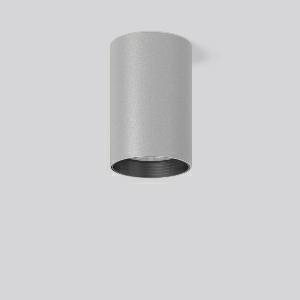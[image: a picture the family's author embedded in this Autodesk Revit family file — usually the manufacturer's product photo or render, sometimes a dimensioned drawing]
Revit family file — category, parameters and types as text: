
# Revit family: heledon_maxi_a_931222_004_1_76_c6c2
name_source: partatom
category: Lighting Fixtures
units: mm (PartAtom-declared; Revit-internal decimal feet)

## family parameters
Cut with Voids When Loaded = No
Host = Face
Light Source = No
Part Type = Normal
Room Calculation Point = No
Round Connector Dimension = Use Diameter
Shared = No

## types (1)
- HELEDON maxi A (1 x LED Modul 940, 2950 lm, 4000)
    Apparent Load = 25 VA
    Approval mark = CE
    CIE Flux Codes = 96 100 100 100 100
    Color Rendering = 92
    Color Temperature = 4000
    Default Elevation = 1800 mm
    Description = Series: HELEDON maxi
Cylindrical surface-mounted downlight. Housing: die-cast aluminium, powder-coated. Internal ceiling frame polycarbonate with bayonet mounting. Black plastic ring and recessed LED to prevent glare from the side. Optical assembly with lens made of plastic (polycarbonate) for the best homogeneous light distribution - can be changed without tools. Best colour rendering index Ra>90. Suitable for Ceiling mounting. Easy installation with a separate ceiling frame with bayonet mounting and plug connection. Driver integrated. Connected via plug-in connector. High quality converter without flickering and stroboscopic effect. The following accessories can be mounted without use of tools: interchangeable lenses, decorative glasses, honeycomb louvre, clear and frosted diffusers, white interchangeable plastic ring. 
Colour: silver
Diameter: 123 mm
Height: 183 mm
Lamp: LED
Socket: without socket
Colour temperature: 4000K
Colour rendering index (CRI): 92
System power: 25 W
Rated luminous flux: 2950 lm
Luminous efficiency: 118 lm/W
Control gear: Converter, dimmable, DALI
Protection class: I
Type of protection: IP 20
    Height = 183 mm
    Lamp = 1 x LED Modul 940
    Lamp Light Flux = 2950 lm
    Lamp count = 1
    Length = 123 mm
    Lifetime = 50000 h
    Luminous efficacy = 118 lm/W
    Manufacturer = RZB
    ModVariant = No
    Model = 931222.004.1.76
    Mounting Place = Ceiling
    Mounting Type = Surface mounted
    Number of Poles = 1
    OnlyDefault = Yes
    Power Factor = 1
    Product Name = HELEDON maxi A
    Product group = Surface mounted downlights
    ProductGroupID = 302
    Protection Class = Protection class I
    Protection Degree = IP 20
    RLX_Detail_Level = 1
    RLX_Emergency_Light_Flux = 0 lm
    RLX_Emergency_Type = 0
    RLX_Emergency_Type_DB = No
    RlxData = <blob elided: 99333 chars, md5=4107362c>
    Socket = socket
    Standby Power = 0 W
    System Light Flux = 2950 lm
    System Power = 25 W
    Type Comments = Product without accessories
    Type Image = 931193.004.jpg
    URL = http://relux.com
    VarID = ---
    Voltage = 230 V
    Voltage Range = 220-240 V
    Weight = 0.00 kg
    Width = 0 mm  [stored 0 ft]

note: [stored X ft] marks values corroborated as IEEE doubles in the binary element streams (Revit-internal decimal feet)

## geometry (parser evidence)
native form markers: Blend x4, Sweep x10
no freeform markers — native parametric forms only
